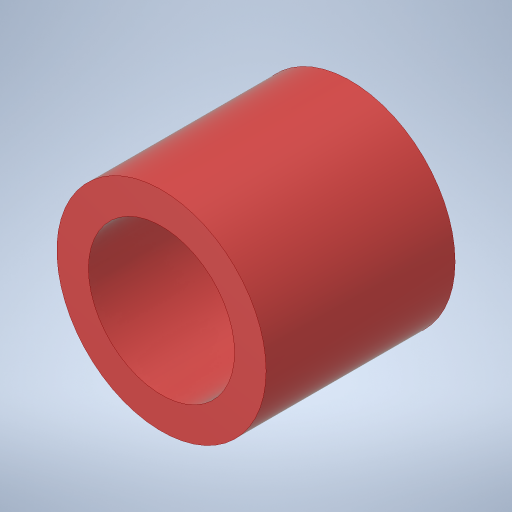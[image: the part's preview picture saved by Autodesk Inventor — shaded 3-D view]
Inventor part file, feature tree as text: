
AUTODESK INVENTOR PART (.ipt)
format: ipt  version: 2023.4 (Build 274418000, 418)  size: 233,472 bytes
history: native  units: in
note: dims shown in document units (in); Inventor stores cm internally (conversion verified against a paired STEP export)
features: extrude x1
ambient origin geometry x8: Origin, YZ Plane, XZ Plane, XY Plane, X Axis, Y Axis, Z Axis, Center Point
bodies: Solid1 (feature_tree)
feature tree (1):
  extrude  "Extrusion1"  TaperAngle=0.0deg  [1 undecoded]
note: 1 required parameter value undecoded (feature->parameter linkage not recoverable at this tier; creation-order binding heuristic only, values carry confidence <= 0.55)
